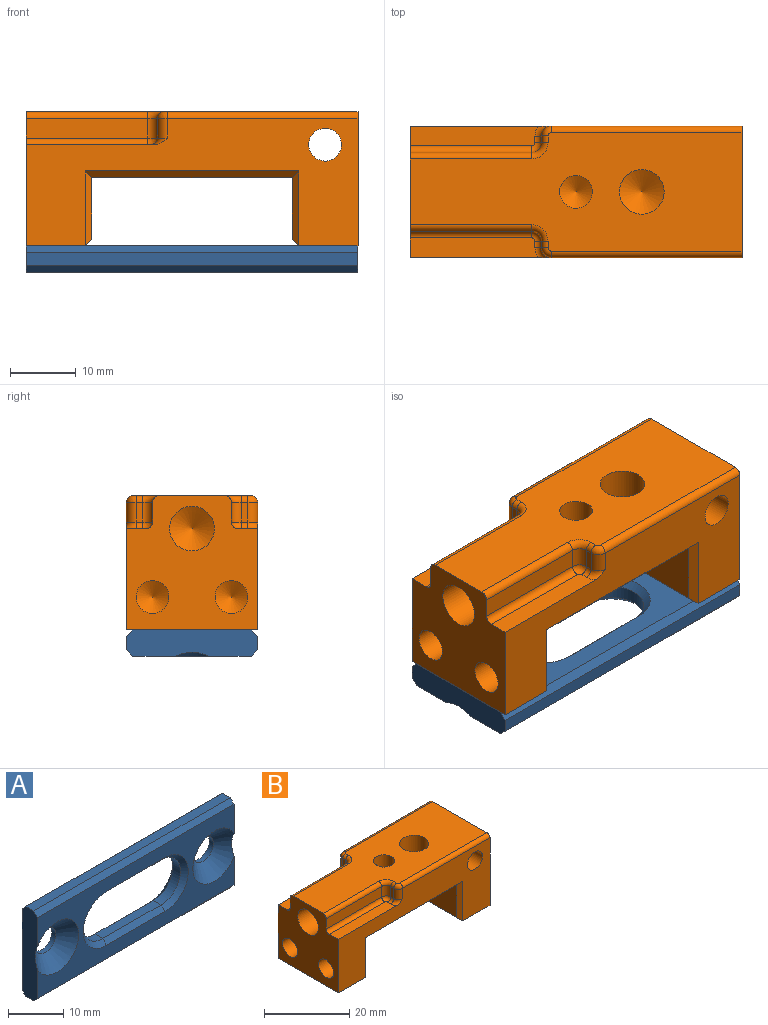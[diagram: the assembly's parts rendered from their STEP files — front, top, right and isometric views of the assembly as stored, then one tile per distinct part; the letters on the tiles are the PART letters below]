
ASSEMBLY  parts=2 mates=1
PART A: 26 faces, bbox 51.7x4x20 mm
  f0: plane 50.5x18mm, normal (0,-1,0), area 422.9mm2, adj f2,f3,f7,f8,f18,f19,f20,f21
  f1: plane 50.5x18mm, normal (0,1,0), area 571.8mm2, adj f2,f3,f6,f9,f14,f15,f16,f17
  f2: plane 20x4mm, normal (-1,0,0), area 76mm2, adj f0,f1,f4,f5,f8,f22,f23,f24
  f3: plane 20x4mm, normal (1,0,0), area 76mm2, adj f0,f1,f4,f5,f7,f22,f23,f24
  f4: plane 50.5x2mm, normal (0,0,1), area 101mm2, adj f2,f3,f22,f24
  f5: plane 50.5x2mm, normal (0,0,-1), area 101mm2, adj f2,f3,f23,f25
  f6: cylinder r=2.65mm len=5.3mm, axis (0,-1,0), area 17.5mm2, adj f1,f7
  f7: cone r=2.65mm half-angle=45deg, axis (0,-1,0), area 105.2mm2, adj f0,f3,f6
  f8: cone r=2.65mm half-angle=45deg, axis (0,-1,0), area 105.2mm2, adj f0,f2,f9
  f9: cylinder r=2.65mm len=5.3mm, axis (0,-1,0), area 17.5mm2, adj f1,f8
  f10: plane 15x2mm, normal (0,0,-1), area 30mm2, adj f11,f13,f17,f21
  f11: cylinder r=5mm len=10mm, axis (0,-1,0), area 31.4mm2, adj f10,f12,f15,f19
  f12: plane 15x2mm, normal (0,0,1), area 30mm2, adj f11,f13,f14,f18
  f13: cylinder r=5mm len=10mm, axis (0,-1,0), area 31.4mm2, adj f10,f12,f16,f20
  f14: plane 15x1mm, normal (0,0.71,0.71), area 21.2mm2, adj f1,f12,f15,f16
  f15: cone r=6mm half-angle=45deg, axis (0,1,0), area 24.4mm2, adj f1,f11,f14,f17
  f16: cone r=6mm half-angle=45deg, axis (0,1,0), area 24.4mm2, adj f1,f13,f14,f17
  f17: plane 15x1mm, normal (0,0.71,-0.71), area 21.2mm2, adj f1,f10,f15,f16
  f18: plane 15x1mm, normal (0,-0.71,0.71), area 21.2mm2, adj f0,f12,f19,f20
  f19: cone r=5mm half-angle=45deg, axis (0,-1,0), area 24.4mm2, adj f0,f11,f18,f21
  f20: cone r=5mm half-angle=45deg, axis (0,-1,0), area 24.4mm2, adj f0,f13,f18,f21
  f21: plane 15x1mm, normal (0,-0.71,-0.71), area 21.2mm2, adj f0,f10,f19,f20
  f22: plane 50.5x1mm, normal (0,0.71,0.71), area 71.4mm2, adj f1,f2,f3,f4
  f23: plane 50.5x1mm, normal (0,0.71,-0.71), area 71.4mm2, adj f1,f2,f3,f5
  f24: plane 50.5x1mm, normal (0,-0.71,0.71), area 71.4mm2, adj f0,f2,f3,f4
  f25: plane 50.5x1mm, normal (0,-0.71,-0.71), area 71.4mm2, adj f0,f2,f3,f5
PART B: 65 faces, bbox 50.5x23.9x20.4 mm
  f0: plane 20.4x20mm, normal (-1,0,0), area 292.4mm2, adj f1,f2,f8,f9,f15,f17,f19,f29
  f1: plane 50.5x18mm, normal (0,0,1), area 687.6mm2, adj f0,f7,f26,f28,f55,f56,f57,f58
  f2: plane 20x9mm, normal (0,0,-1), area 166.1mm2, adj f0,f8,f9,f23,f41
  f3: plane 18x9.4mm, normal (1,0,0), area 169.2mm2, adj f4,f39,f41,f43
  f4: plane 30.5x18mm, normal (0,0,-1), area 549mm2, adj f3,f5,f40,f45
  f5: plane 18x9.4mm, normal (-1,0,0), area 169.2mm2, adj f4,f42,f44,f46
  f6: plane 20x9mm, normal (0,0,-1), area 166.1mm2, adj f7,f8,f9,f21,f44
  f7: plane 20.4x20mm, normal (1,0,0), area 368.3mm2, adj f1,f6,f8,f9,f11,f13,f55,f61
  f8: plane 50.5x19.4mm, normal (0,-1,0), area 504.3mm2, adj f0,f2,f6,f7,f24,f35,f38,f39
  f9: plane 50.5x19.4mm, normal (0,1,0), area 504.3mm2, adj f0,f2,f6,f7,f24,f32,f33,f43
  f10: cone r=0mm half-angle=59deg, axis (1,0,0), area 22.9mm2, adj f11
  f11: cylinder r=2.5mm len=8mm, axis (1,0,0), area 125.7mm2, adj f7,f10
  f12: cone r=0mm half-angle=59deg, axis (1,0,0), area 22.9mm2, adj f13
  f13: cylinder r=2.5mm len=8mm, axis (1,0,0), area 125.7mm2, adj f7,f12
  f14: cone r=0mm half-angle=59deg, axis (-1,0,0), area 22.9mm2, adj f15
  f15: cylinder r=2.5mm len=8mm, axis (-1,0,0), area 125.7mm2, adj f0,f14
  f16: cone r=0mm half-angle=59deg, axis (-1,0,0), area 22.9mm2, adj f17
  f17: cylinder r=2.5mm len=8mm, axis (-1,0,0), area 125.7mm2, adj f0,f16
  f18: cone r=0mm half-angle=59deg, axis (-1,0,0), area 42.4mm2, adj f19
  f19: cylinder r=3.4mm len=19mm, axis (-1,0,0), area 405.9mm2, adj f0,f18
  f20: cone r=0mm half-angle=59deg, axis (0,0,-1), area 16.2mm2, adj f21
  f21: cylinder r=2.1mm len=10mm, axis (0,0,-1), area 131.9mm2, adj f6,f20
  f22: cone r=0mm half-angle=59deg, axis (0,0,-1), area 16.2mm2, adj f23
  f23: cylinder r=2.1mm len=10mm, axis (0,0,-1), area 131.9mm2, adj f2,f22
  f24: cylinder r=2.5mm len=20mm, axis (0,-1,0), area 314.2mm2, adj f8,f9
  f25: cone r=0mm half-angle=59deg, axis (0,0,1), area 42.4mm2, adj f26
  f26: cylinder r=3.4mm len=7mm, axis (0,0,1), area 149.5mm2, adj f1,f25
  f27: cone r=0mm half-angle=59deg, axis (0,0,1), area 22.9mm2, adj f28
  f28: cylinder r=2.5mm len=8mm, axis (0,0,1), area 125.7mm2, adj f1,f27
  f29: plane 18.5x3mm, normal (0,1,0), area 55.5mm2, adj f0,f30,f47,f60
  f30: cylinder r=1.5mm len=3mm, axis (0,0,1), area 7.1mm2, adj f29,f31,f48,f62
  f31: plane 3x1mm, normal (-1,0,0), area 3mm2, adj f30,f32,f49,f64
  f32: cylinder r=1.5mm len=3mm, axis (0,0,1), area 7.1mm2, adj f9,f31,f50,f63
  f33: plane 19.5x3mm, normal (0,0,1), area 57.2mm2, adj f0,f9,f47,f48,f49,f50
  f34: plane 18.5x3mm, normal (0,-1,0), area 55.5mm2, adj f0,f37,f51,f59
  f35: cylinder r=1.5mm len=3mm, axis (0,0,1), area 7.1mm2, adj f8,f36,f54,f56
  f36: plane 3x1mm, normal (-1,0,0), area 3mm2, adj f35,f37,f53,f57
  f37: cylinder r=1.5mm len=3mm, axis (0,0,1), area 7.1mm2, adj f34,f36,f52,f58
  f38: plane 19.5x3mm, normal (0,0,1), area 57.2mm2, adj f0,f8,f51,f52,f53,f54
  f39: plane 11.4x1mm, normal (0.71,-0.71,0), area 14.7mm2, adj f3,f8,f40,f41
  f40: plane 32.5x1mm, normal (0,-0.71,-0.71), area 44.5mm2, adj f4,f8,f39,f42
  f41: plane 20x1mm, normal (0.71,0,-0.71), area 26.9mm2, adj f2,f3,f39,f43
  f42: plane 11.4x1mm, normal (-0.71,-0.71,0), area 14.7mm2, adj f5,f8,f40,f44
  f43: plane 11.4x1mm, normal (0.71,0.71,0), area 14.7mm2, adj f3,f9,f41,f45
  f44: plane 20x1mm, normal (-0.71,0,-0.71), area 26.9mm2, adj f5,f6,f42,f46
  f45: plane 32.5x1mm, normal (0,0.71,-0.71), area 44.5mm2, adj f4,f9,f43,f46
  f46: plane 11.4x1mm, normal (-0.71,0.71,0), area 14.7mm2, adj f5,f9,f44,f45
  f47: cylinder r=1mm len=18.5mm, axis (1,0,0), area 29.1mm2, adj f0,f29,f33,f48
  f48: torus R=0.5mm, axis (0,0,1), area 2.8mm2, adj f30,f33,f47,f49
  f49: cylinder r=1mm len=1mm, axis (0,1,0), area 1.6mm2, adj f31,f33,f48,f50
  f50: torus R=2.5mm, axis (0,0,1), area 2.9mm2, adj f9,f32,f33,f49
  f51: cylinder r=1mm len=18.5mm, axis (-1,0,0), area 29.1mm2, adj f0,f34,f38,f52
  f52: torus R=0.5mm, axis (0,0,1), area 2.8mm2, adj f37,f38,f51,f53
  f53: cylinder r=1mm len=1mm, axis (0,1,0), area 1.6mm2, adj f36,f38,f52,f54
  f54: torus R=2.5mm, axis (0,0,1), area 2.9mm2, adj f8,f35,f38,f53
  f55: cylinder r=1mm len=29mm, axis (1,0,0), area 45.6mm2, adj f1,f7,f8,f56
  f56: torus R=0.5mm, axis (0,0,1), area 2.8mm2, adj f1,f35,f55,f57
  f57: cylinder r=1mm len=1mm, axis (0,-1,0), area 1.6mm2, adj f1,f36,f56,f58
  f58: torus R=2.5mm, axis (0,0,1), area 4.6mm2, adj f1,f37,f57,f59
  f59: cylinder r=1mm len=18.5mm, axis (1,0,0), area 29.1mm2, adj f0,f1,f34,f58
  f60: cylinder r=1mm len=18.5mm, axis (-1,0,0), area 29.1mm2, adj f0,f1,f29,f62
  f61: cylinder r=1mm len=29mm, axis (-1,0,0), area 45.6mm2, adj f1,f7,f9,f63
  f62: torus R=2.5mm, axis (0,0,1), area 4.6mm2, adj f1,f30,f60,f64
  f63: torus R=0.5mm, axis (0,0,1), area 2.8mm2, adj f1,f32,f61,f64
  f64: cylinder r=1mm len=1mm, axis (0,-1,0), area 1.6mm2, adj f1,f31,f62,f63
PLACE A rot(axis=(1,0,0),90deg) t=(0,-10,-20.4)mm
PLACE B at identity
MATE planar A.f1 <-> B.f2  axis (0,0,1) through (0,0,-20.4)mm
